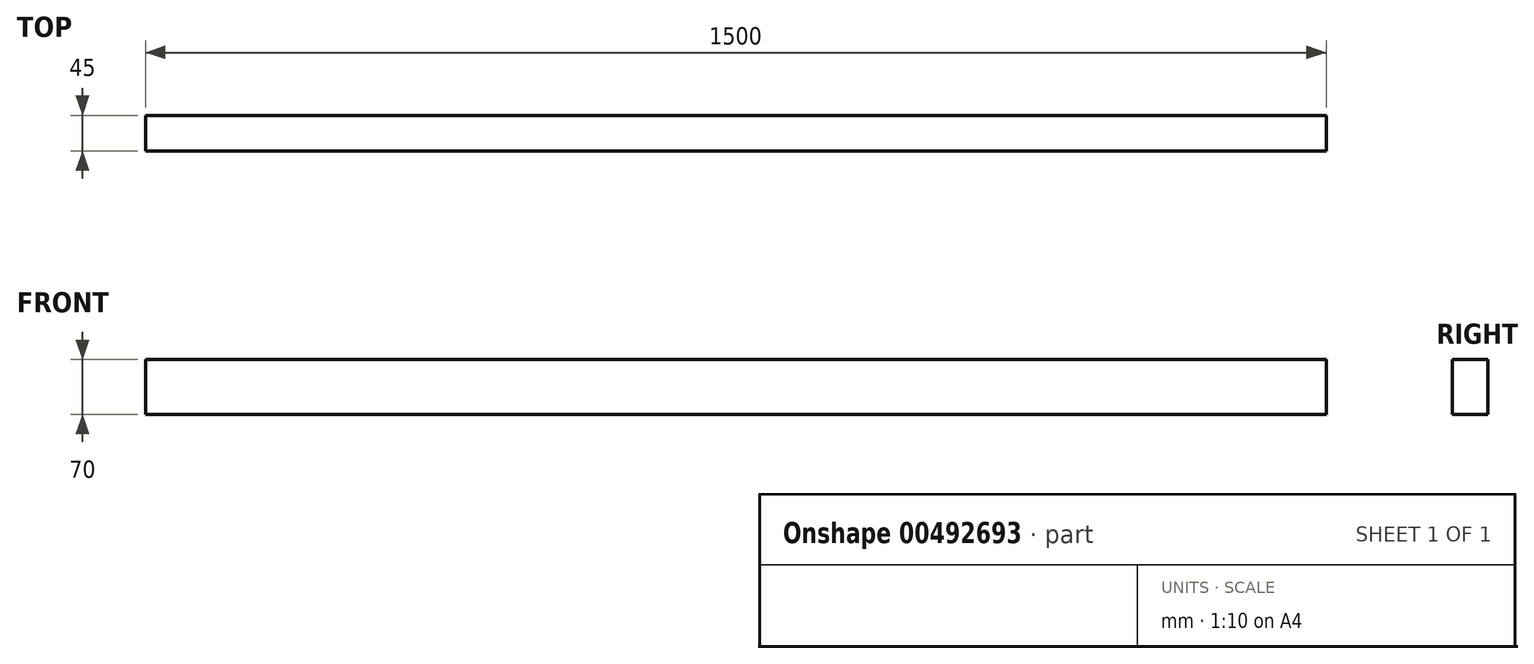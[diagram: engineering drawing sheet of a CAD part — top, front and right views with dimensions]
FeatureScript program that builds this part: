
annotation { "Feature Type Name" : "Feature", "Feature Type Description" : "" }
export const myFeature = defineFeature(function(context is Context, id is Id, definition is map)
    precondition{}
    {
        {
            var Q0;
            Q0=qCreatedBy(makeId("Front.planeOp"),FACE);
            var sketch = newSketch(context, id + "F0", { "sketchPlane" : qUnion([Q0])});
            skLineSegment(sketch, "E0.bottom", {"start": v(0, 0) * mm, "end": v(-1500, 0) * mm});
            skLineSegment(sketch, "E0.top", {"start": v(0, 70) * mm, "end": v(-1500, 70) * mm});
            skLineSegment(sketch, "E0.left", {"start": v(0, 0) * mm, "end": v(0, 70) * mm});
            skLineSegment(sketch, "E0.right", {"start": v(-1500, 0) * mm, "end": v(-1500, 70) * mm});
            skSolve(sketch);
        }
        {
            var Q0;
            Q0 = qSketchRegion(id + "F0", true);
            extrude(context, id + "F1", {"entities" : qUnion([Q0]), "depth" : 45 * mm});
        }
    });
